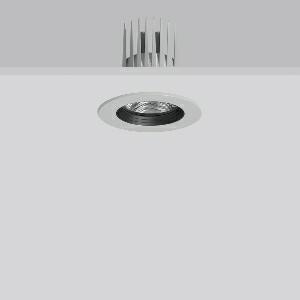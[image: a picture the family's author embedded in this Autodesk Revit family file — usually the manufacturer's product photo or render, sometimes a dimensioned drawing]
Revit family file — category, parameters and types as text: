
# Revit family: heledon_mini_e_901741_004_3_76_f87d
name_source: partatom
category: Lighting Fixtures
units: mm (PartAtom-declared; Revit-internal decimal feet)

## family parameters
Cut with Voids When Loaded = No
Host = Face
Light Source = No
Part Type = Normal
Room Calculation Point = No
Round Connector Dimension = Use Diameter
Shared = No

## types (1)
- HELEDON mini E (1 x LED Modul 935, 2500 lm, 3500)
    Apparent Load = 20 VA
    Approval mark = CE
    CIE Flux Codes = 99 100 100 100 100
    Color Rendering = 92
    Color Temperature = 3500
    Default Elevation = 1800 mm
    Description = Series: HELEDON mini
Round recessed downlight. Housing: die-cast aluminium, powder-coated. Black plastic ring and recessed LED to prevent glare from the side. Optical assembly with reflector made of MIRO-Silver with 98% total light reflection for outstanding efficiency - can be changed without tools. Best colour rendering index Ra>90. Suitable for Recessed ceiling mounting. Installation without tools thanks to spring fastening system. Including separate LED converter with connecting cable 600 mm.High quality converter without flickering and stroboscopic effect. Through-wiring box (5 pole) available as accessory. The following accessories can be mounted without use of tools: interchangeable lenses, decorative glasses, honeycomb louvre, clear and frosted diffusers, white interchangeable plastic ring. 
Colour: silver
Diameter: 124 mm
Height: 3 mm
Cut-out diameter: 114 mm
Recess height: 170 mm
Luminaire: recess height: 120 mm
Lamp: LED
Socket: without socket
Colour temperature: 3500K
Colour rendering index (CRI): 92
System power: 20 W
Rated luminous flux: 2500 lm
Luminous efficiency: 125 lm/W
Control gear: Converter, dimmable, DALI
Protection class: II
Type of protection: IP 20
    Height = 0 mm  [stored 0 ft]
    Lamp = 1 x LED Modul 935
    Lamp Light Flux = 2500 lm
    Lamp count = 1
    Length = 124 mm  [stored 0.406824 ft]
    Lifetime = 50000 h
    Luminous efficacy = 125 lm/W
    Manufacturer = RZB
    ModVariant = No
    Model = 901741.004.3.76
    Mounting Place = Ceiling
    Mounting Type = Recessed
    Number of Poles = 1
    OnlyDefault = Yes
    Power Factor = 1
    Product Name = HELEDON mini E
    Product group = Recessed downlights
    ProductGroupID = 402
    Protection Class = Protection class II
    Protection Degree = IP 20
    RLX_Detail_Level = 1
    RLX_Emergency_Light_Flux = 0 lm
    RLX_Emergency_Type = 0
    RLX_Emergency_Type_DB = No
    RlxData = <blob elided: 128001 chars, md5=c8d1929c>
    Socket = socket
    Standby Power = 0 W
    System Light Flux = 2500 lm
    System Power = 20 W
    Type Comments = Product without accessories
    Type Image = 901657.004.jpg
    URL = http://relux.com
    VarID = ---
    Voltage = 230 V
    Voltage Range = 220-240 V
    Weight = 0.00 kg
    Width = 0 mm  [stored 0 ft]

note: [stored X ft] marks values corroborated as IEEE doubles in the binary element streams (Revit-internal decimal feet)

## geometry (parser evidence)
native form markers: Blend x4, Sweep x11
no freeform markers — native parametric forms only
